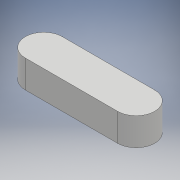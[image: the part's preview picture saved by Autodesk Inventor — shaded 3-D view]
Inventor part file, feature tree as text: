
AUTODESK INVENTOR PART (.ipt)
format: ipt  version: 2018 (Build 220112000, 112)  size: 90,624 bytes
history: native  units: mm
features: extrude x1, sketch x1
ambient origin geometry x8: Origin, YZ Plane, XZ Plane, XY Plane, X Axis, Y Axis, Z Axis, Center Point
bodies: Body1 (feature_tree)
feature tree (2):
  extrude  "Extrusión2"  Depth=8.0mm
  sketch  "Boceto1"  dims[d16=6.0mm d17=0.0mm d25=8.0mm d26=20.0mm]
